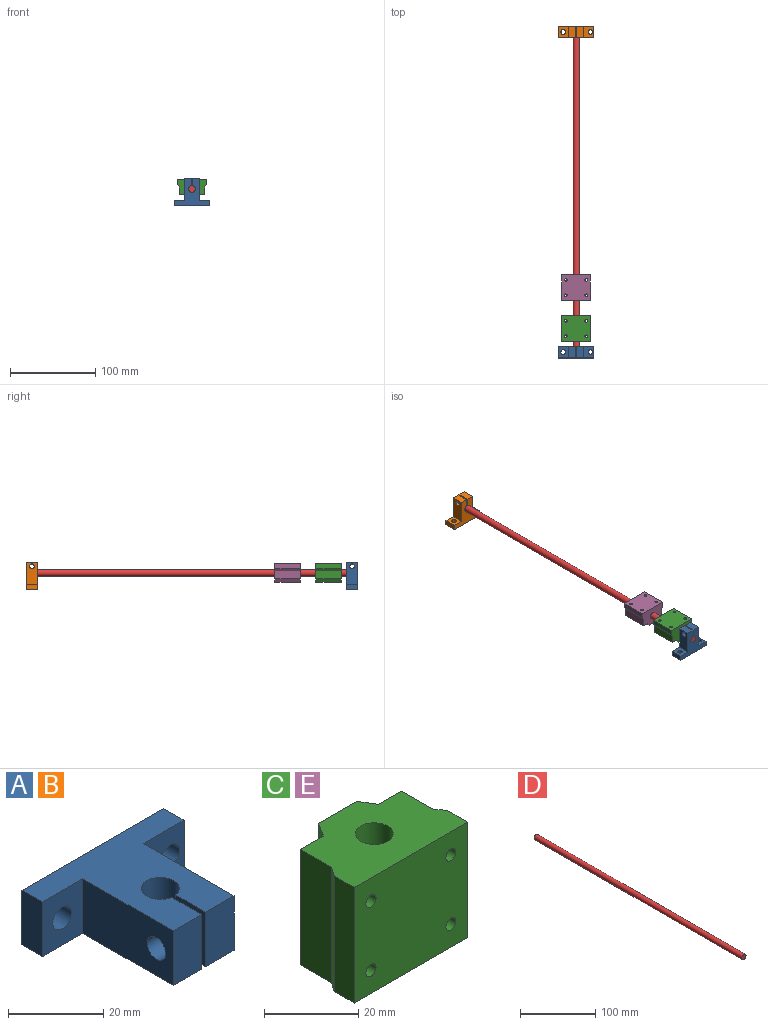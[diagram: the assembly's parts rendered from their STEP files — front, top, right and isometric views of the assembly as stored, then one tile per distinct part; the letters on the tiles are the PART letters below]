
ASSEMBLY  parts=5 mates=4
PART A: 18 faces, bbox 42x32.8x14 mm
  f0: plane 42x14mm, normal (0,1,0), area 540.5mm2, adj f1,f11,f12,f13,f14,f15
  f1: plane 14x6mm, normal (1,0,0), area 84mm2, adj f0,f2,f12,f13
  f2: plane 14x12mm, normal (0,-1,0), area 144.2mm2, adj f1,f3,f12,f13,f15
  f3: plane 26.8x14mm, normal (1,0,0), area 351.4mm2, adj f2,f4,f12,f13,f16
  f4: plane 14x8.4mm, normal (0,-1,0), area 117.6mm2, adj f3,f5,f12,f13
  f5: plane 14x8.85mm, normal (-1,0,0), area 100.1mm2, adj f4,f6,f12,f13,f16
  f6: cylinder r=4mm len=14mm, axis (0,0,1), area 335mm2, adj f5,f7,f12,f13
  f7: plane 14x8.85mm, normal (1,0,0), area 100.1mm2, adj f6,f8,f12,f13,f17
  f8: plane 14x8.4mm, normal (0,-1,0), area 117.6mm2, adj f7,f9,f12,f13
  f9: plane 26.8x14mm, normal (-1,0,0), area 351.4mm2, adj f8,f10,f12,f13,f17
  f10: plane 14x12mm, normal (0,-1,0), area 144.2mm2, adj f9,f11,f12,f13,f14
  f11: plane 14x6mm, normal (-1,0,0), area 84mm2, adj f0,f10,f12,f13
  f12: plane 42x32.8mm, normal (0,0,-1), area 673.6mm2, adj f0,f1,f2,f3,f4,f5,f6,f7
  f13: plane 42x32.8mm, normal (0,0,1), area 673.6mm2, adj f0,f1,f2,f3,f4,f5,f6,f7
  f14: cylinder r=2.75mm len=6mm, axis (0,-1,0), area 103.7mm2, adj f0,f10
  f15: cylinder r=2.75mm len=6mm, axis (0,-1,0), area 103.7mm2, adj f0,f2
  f16: cylinder r=2.75mm len=8.4mm, axis (1,0,0), area 145.1mm2, adj f3,f5
  f17: cylinder r=2.75mm len=8.4mm, axis (-1,0,0), area 145.1mm2, adj f7,f9
PART B: same geometry as A
PART C: 19 faces, bbox 34x22x30 mm
  f0: plane 34x30mm, normal (0,-1,0), area 991mm2, adj f1,f12,f13,f14,f15,f16,f17,f18
  f1: plane 30x6mm, normal (-1,0,0), area 180mm2, adj f0,f2,f13,f14
  f2: plane 30x2.67mm, normal (-0.82,0.57,0), area 97.1mm2, adj f1,f3,f13,f14
  f3: plane 30x9.33mm, normal (-1,0,0), area 280mm2, adj f2,f4,f13,f14
  f4: plane 30x6.93mm, normal (0,1,0), area 193.5mm2, adj f3,f5,f13,f14,f15,f16
  f5: plane 30x4mm, normal (-0.85,0.53,0), area 141.3mm2, adj f4,f6,f13,f14
  f6: plane 30x11.5mm, normal (0,1,0), area 344.9mm2, adj f5,f7,f13,f14
  f7: plane 30x4mm, normal (0.85,0.53,0), area 141.3mm2, adj f6,f8,f13,f14
  f8: plane 30x6.93mm, normal (0,1,0), area 193.5mm2, adj f7,f9,f13,f14,f17,f18
  f9: plane 30x9.33mm, normal (1,0,0), area 280mm2, adj f8,f10,f13,f14
  f10: plane 30x2.67mm, normal (0.82,0.57,0), area 97.1mm2, adj f9,f12,f13,f14
  f11: cylinder r=4mm len=30mm, axis (0,0,-1), area 754mm2, adj f13,f14
  f12: plane 30x6mm, normal (1,0,0), area 180mm2, adj f0,f10,f13,f14
  f13: plane 34x22mm, normal (0,0,1), area 578.6mm2, adj f0,f1,f2,f3,f4,f5,f6,f7
  f14: plane 34x22mm, normal (0,0,-1), area 578.6mm2, adj f0,f1,f2,f3,f4,f5,f6,f7
  f15: cylinder r=1.52mm len=18mm, axis (0,1,0), area 171.9mm2, adj f0,f4
  f16: cylinder r=1.52mm len=18mm, axis (0,1,0), area 171.9mm2, adj f0,f4
  f17: cylinder r=1.52mm len=18mm, axis (0,1,0), area 171.9mm2, adj f0,f8
  f18: cylinder r=1.52mm len=18mm, axis (0,1,0), area 171.9mm2, adj f0,f8
PART D: 3 faces, bbox 8x390x8 mm
  f0: cylinder r=4mm len=390mm, axis (0,-1,0), area 9801.8mm2, adj f1,f2
  f1: plane 8x8mm, normal (0,1,0), area 50.3mm2, adj f0
  f2: plane 8x8mm, normal (0,-1,0), area 50.3mm2, adj f0
PART E: same geometry as C
PLACE A rot(axis=(-1,0,0),90deg) t=(43.65,-13.91,51.72)mm
PLACE B rot(axis=(-1,0,0),90deg) t=(43.65,362.09,51.72)mm
PLACE C rot(axis=(0,-0.71,0.71),180deg) t=(-37.52,21.59,51.19)mm
PLACE D t=(50.78,-27.91,41.77)mm
PLACE E rot(axis=(0,-0.71,0.71),180deg) t=(-37.52,69.71,51.19)mm
MATE fastened D.f0 <-> A.f6  axis (0,-1,0) through (-1.84,-27.91,89.39)mm
MATE slider D.f0 <-> E.f11  axis (0,-1,0) through (-1.84,27.09,89.39)mm
MATE fastened D.f0 <-> B.f6  axis (0,1,0) through (-1.84,362.09,89.39)mm
MATE slider D.f0 <-> C.f11  axis (0,-1,0) through (-1.84,-12.91,89.39)mm
